# Revit family: Table-Teknion-CTTS_Square_Table-R2021
name_source: partatom
category: Furniture
units: mm (PartAtom-declared; Revit-internal decimal feet)

## family parameters
Always vertical = Yes
Cut with Voids When Loaded = No
OmniClass Number = 23.40.20.00
OmniClass Title = General Furniture and Specialties
Room Calculation Point = No
Shared = Yes
Work Plane-Based = No

## types (3) — shared parameters
Assembly Code = E2020200
Manufacturer = Teknion
Manufacturer Fax = 416.661.4586
Part Number = CTTS
Product Documentation Link = https://www.teknion.com
Product Line = Chronicle
Product Page URL = https://www.teknion.com
Series = Chronicle
Sustainability Data = https://www.teknion.com
URL = www.teknion.com
Unit Weight URL = http://www.teknion.com
Warranty = http://www.teknion.com
zero-valued in all types: Default Elevation

## per-type parameters (varying)
| type | Description | Length | Model | Size |
| Size 48 | Square Table, Size 48" | 67.882 " | CTTS48 | 48 " |
| Size 42 | Square Table, Size 42" | 59.397 " | CTTS42 | 42 " |
| Size 36 | Square Table, Size 36" | 50.912 " | CTTS36 | 36 " |

## geometry (parser evidence)
native form markers: Sweep x3
no freeform markers — native parametric forms only
